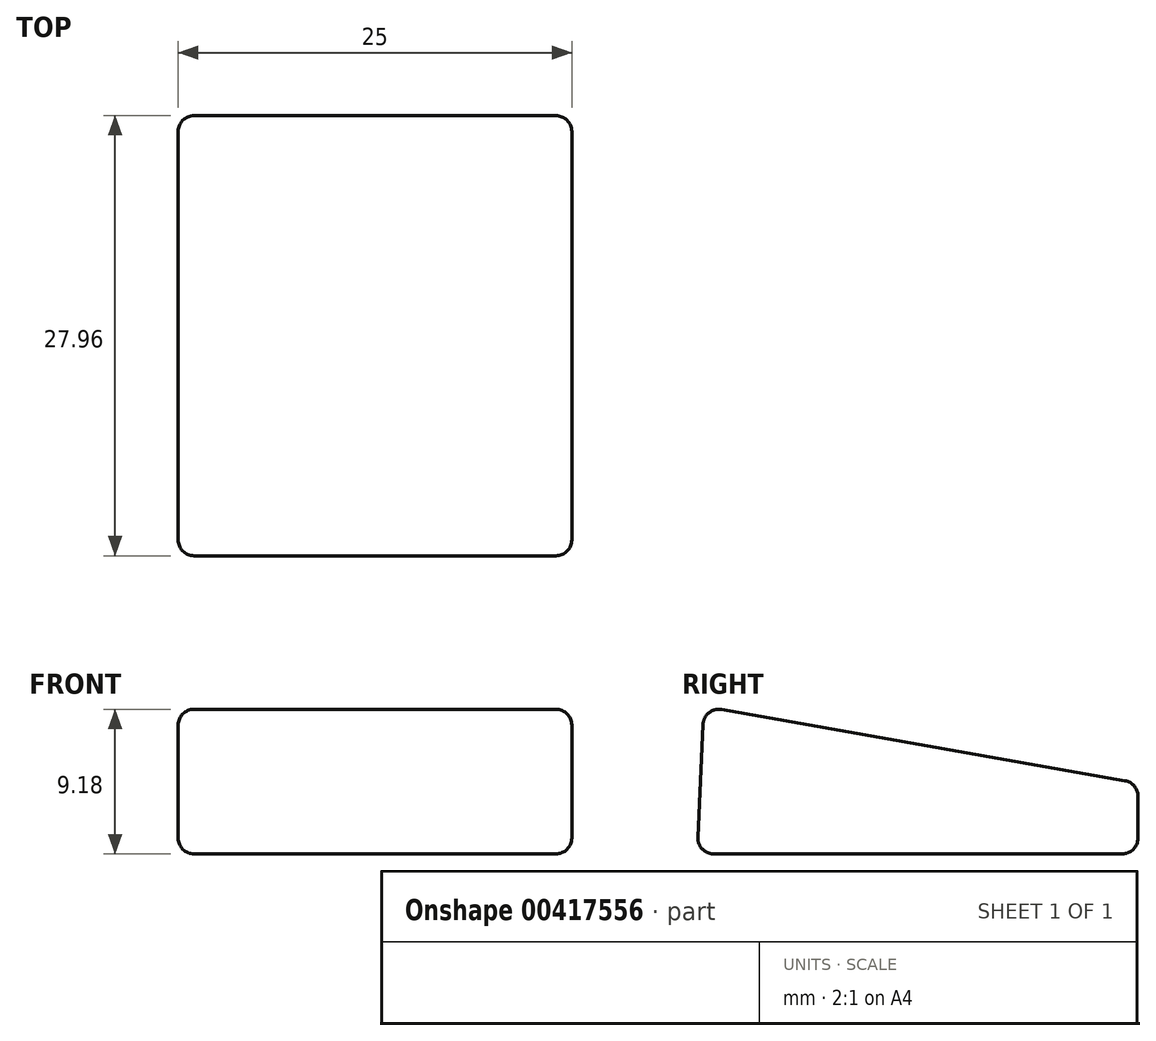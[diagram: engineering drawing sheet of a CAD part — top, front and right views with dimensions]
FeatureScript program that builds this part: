
annotation { "Feature Type Name" : "Feature", "Feature Type Description" : "" }
export const myFeature = defineFeature(function(context is Context, id is Id, definition is map)
    precondition{}
    {
        {
            var Q0;
            Q0=qCreatedBy(makeId("Right.planeOp"),FACE);
            var sketch = newSketch(context, id + "F0", { "sketchPlane" : qUnion([Q0])});
            skLineSegment(sketch, "E0", {"start": v(-9.41, 0) * mm, "end": v(18.59, 0) * mm});
            skLineSegment(sketch, "E1", {"start": v(18.59, 0) * mm, "end": v(18.59, 4.5) * mm});
            skLineSegment(sketch, "E2", {"start": v(18.59, 4.5) * mm, "end": v(-8.99, 9.36) * mm});
            skLineSegment(sketch, "E3", {"start": v(-8.99, 9.36) * mm, "end": v(-9.41, 0) * mm});
            skSolve(sketch);
        }
        {
            var Q0;
            Q0=makeQuery(id+"F0.imprint","IMPRINT",FACE,{"disambiguationData":[TD([[makeQuery(id+"F0.imprint","IMPRINT",EDGE,{"derivedFrom":sQuery(id+"F0.wireOp",EDGE,"E0")}),1.0]])]});
            extrude(context, id + "F1", {"entities" : qUnion([Q0]), "depth" : 25 * mm});
        }
        {
            var Q0;
            Q0=makeQuery(id+"F1.opExtrude","SWEPT_FACE",FACE,{"disambiguationData":[OSD([sQuery(id+"F0.wireOp",EDGE,"E2")])]});
            var Q1;
            Q1=makeQuery(id+"F1.opExtrude","SWEPT_FACE",FACE,{"disambiguationData":[OSD([sQuery(id+"F0.wireOp",EDGE,"E0")])]});
            var Q2;
            Q2=makeQuery(id+"F1.opExtrude","CAP_EDGE",EDGE,{"disambiguationData":[OSD([sQuery(id+"F0.wireOp",EDGE,"E3")])],"isStart":false});
            var Q3;
            Q3=makeQuery(id+"F1.opExtrude","CAP_EDGE",EDGE,{"disambiguationData":[OSD([sQuery(id+"F0.wireOp",EDGE,"E3")])],"isStart":true});
            var Q4;
            Q4=makeQuery(id+"F1.opExtrude","CAP_EDGE",EDGE,{"disambiguationData":[OSD([sQuery(id+"F0.wireOp",EDGE,"E1")])],"isStart":false});
            var Q5;
            Q5=makeQuery(id+"F1.opExtrude","CAP_EDGE",EDGE,{"disambiguationData":[OSD([sQuery(id+"F0.wireOp",EDGE,"E1")])],"isStart":true});
            fillet(context, id + "F2", {"entities" : qUnion([Q0, Q1, Q2, Q3, Q4, Q5]), "radius" : 1 * mm, "tangentPropagation" : true, "allowEdgeOverflow" : false});
        }
    });
